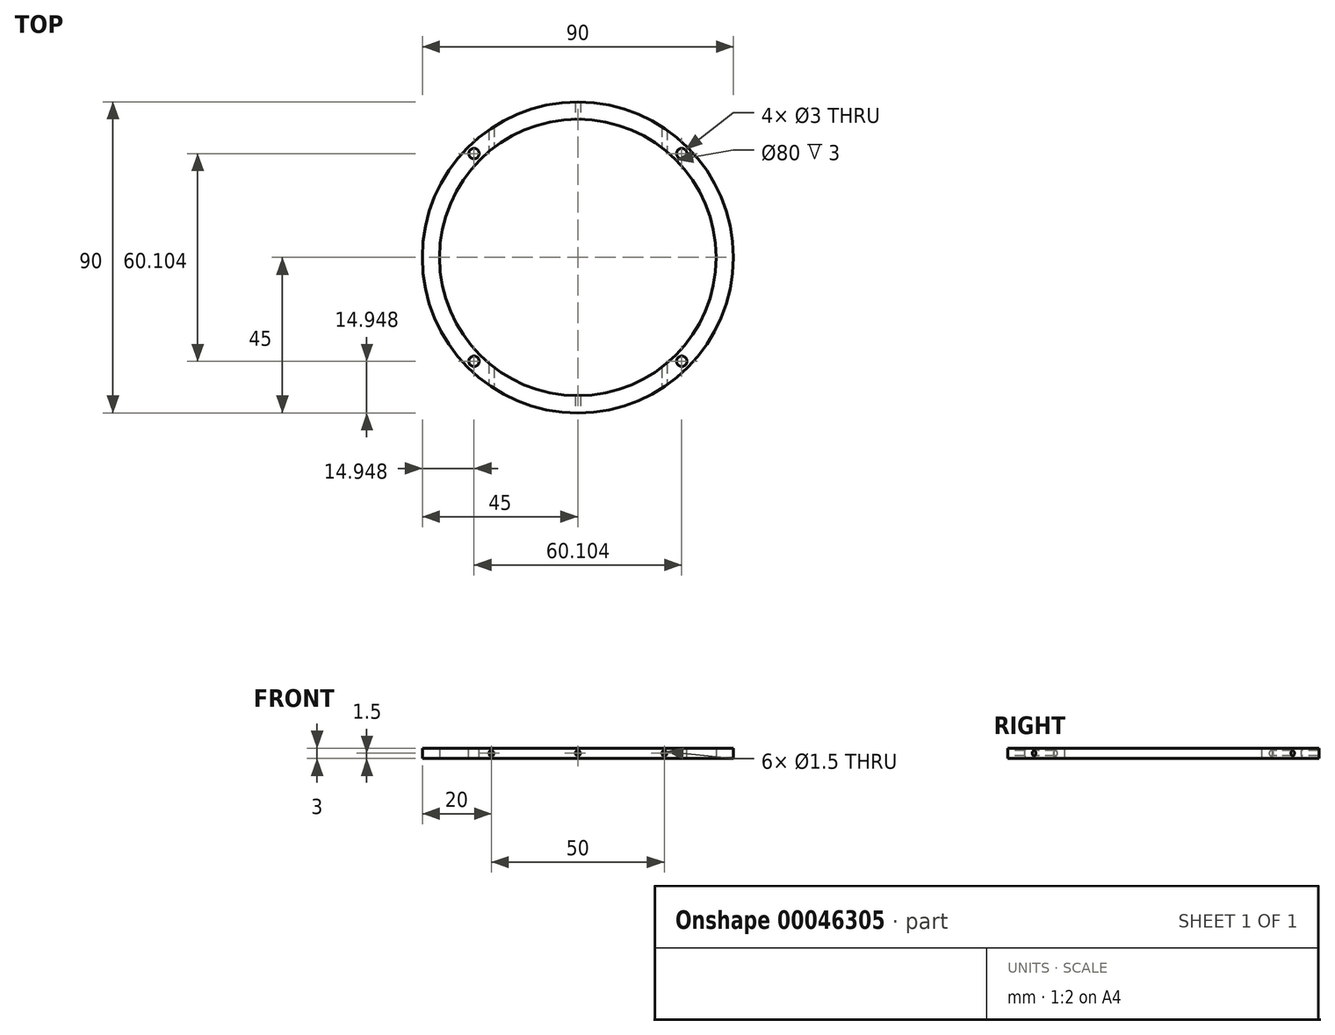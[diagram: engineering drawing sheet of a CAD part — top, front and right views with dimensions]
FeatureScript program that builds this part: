
annotation { "Feature Type Name" : "Feature", "Feature Type Description" : "" }
export const myFeature = defineFeature(function(context is Context, id is Id, definition is map)
    precondition{}
    {
        {
            var Q0;
            Q0=qCreatedBy(makeId("Top.planeOp"),FACE);
            var sketch = newSketch(context, id + "F0", { "sketchPlane" : qUnion([Q0])});
            skCircle(sketch, "E0", {"center": v(0, 0) * mm, "radius": 45 * mm});
            skCircle(sketch, "E1", {"center": v(0, 0) * mm, "radius": 40 * mm});
            skSolve(sketch);
        }
        {
            var Q0;
            Q0=qCreatedBy(makeId("Top.planeOp"),FACE);
            cPlane(context, id + "F1", {"entities" : qUnion([Q0]), "cplaneType" : CPlaneType.OFFSET, "offset" : 1.5 * mm, "width" : 150 * mm, "height" : 150 * mm});
        }
        {
            var Q0;
            Q0=makeQuery(id+"F0.imprint","IMPRINT",FACE,{"disambiguationData":[TD([[makeQuery(id+"F0.imprint","IMPRINT",EDGE,{"derivedFrom":sQuery(id+"F0.wireOp",EDGE,"E0")}),1.0]])]});
            extrude(context, id + "F2", {"entities" : qUnion([Q0]), "depth" : 3 * mm});
        }
        {
            var Q0;
            Q0=qCreatedBy(id+"F1.planeOp",FACE);
            var sketch = newSketch(context, id + "F3", { "sketchPlane" : qUnion([Q0])});
            skLineSegment(sketch, "E2.bottom", {"start": v(-0.75, 45) * mm, "end": v(0.75, 45) * mm});
            skLineSegment(sketch, "E2.top", {"start": v(-0.75, -45) * mm, "end": v(0.75, -45) * mm});
            skLineSegment(sketch, "E2.left", {"start": v(-0.75, 45) * mm, "end": v(-0.75, -45) * mm});
            skLineSegment(sketch, "E2.right", {"start": v(0.75, 45) * mm, "end": v(0.75, -45) * mm});
            skLineSegment(sketch, "E3.1.0.0", {"start": v(-24.25, 45) * mm, "end": v(-24.25, -45) * mm});
            skLineSegment(sketch, "E3.1.0.1", {"start": v(-25.75, 45) * mm, "end": v(-25.75, -45) * mm});
            skLineSegment(sketch, "E3.1.0.2", {"start": v(-25.75, -45) * mm, "end": v(-24.25, -45) * mm});
            skLineSegment(sketch, "E3.1.0.3", {"start": v(-25.75, 45) * mm, "end": v(-24.25, 45) * mm});
            skLineSegment(sketch, "E3.direction1", {"start": v(-24.25, -45) * mm, "end": v(0.75, -45) * mm, "construction": true});
            skLineSegment(sketch, "E4.1.0.0", {"start": v(24.25, 45) * mm, "end": v(24.25, -45) * mm});
            skLineSegment(sketch, "E4.1.0.1", {"start": v(25.75, 45) * mm, "end": v(25.75, -45) * mm});
            skLineSegment(sketch, "E4.1.0.2", {"start": v(24.25, 45) * mm, "end": v(25.75, 45) * mm});
            skLineSegment(sketch, "E4.1.0.3", {"start": v(24.25, -45) * mm, "end": v(25.75, -45) * mm});
            skLineSegment(sketch, "E4.direction1", {"start": v(-0.75, -45) * mm, "end": v(24.25, -45) * mm, "construction": true});
            skSolve(sketch);
        }
        {
            var Q0;
            {var subQ0=sQuery(id+"F0.wireOp",EDGE,"E0");var subQ1=sQuery(id+"F0.wireOp",EDGE,"E1");Q0=makeQuery(id+"F0FMnj3Zhg4bKZp_1.boolean.opBoolean","SPLIT",FACE,{"disambiguationData":[TD([makeQuery(id+"F2.opExtrude","SWEPT_FACE",FACE,{"disambiguationData":[OSD([subQ0])]}),makeQuery(id+"F2.opExtrude","SWEPT_FACE",FACE,{"disambiguationData":[OSD([subQ1])]}),makeQuery(id+"F0FMnj3Zhg4bKZp_1.opExtrude","SWEPT_FACE",FACE,{"disambiguationData":[OSD([sQuery(id+"F3.wireOp",EDGE,"E3.1.0.1")])]})])],"derivedFrom":makeQuery(id+"F2.opExtrude","CAP_FACE",FACE,{"disambiguationData":[OSD([subQ0,subQ1])],"isStart":false})});}
            var sketch = newSketch(context, id + "F4", { "sketchPlane" : qUnion([Q0])});
            skCircle(sketch, "E5", {"center": v(0, 0) * mm, "radius": 42.5 * mm, "construction": true});
            skLineSegment(sketch, "E6", {"start": v(-30.05, 30.05) * mm, "end": v(30.05, -30.05) * mm, "construction": true});
            skLineSegment(sketch, "E7", {"start": v(-30.05, -30.05) * mm, "end": v(30.05, 30.05) * mm, "construction": true});
            skSolve(sketch);
        }
        {
            var Q0;
            Q0=sQuery(id+"F4.wireOp",VERTEX,"E6.start");
            var Q1;
            Q1=sQuery(id+"F4.wireOp",VERTEX,"E7.start");
            var Q2;
            Q2=sQuery(id+"F4.wireOp",VERTEX,"E6.end");
            var Q3;
            Q3=sQuery(id+"F4.wireOp",VERTEX,"E7.end");
            var Q4;
            Q4=makeQuery(id+"F2.opExtrude","SWEPT_BODY",BODY,{"disambiguationData":[OSD([sQuery(id+"F0.wireOp",EDGE,"E0"),sQuery(id+"F0.wireOp",EDGE,"E1")])]});
            hole(context, id + "F5", {"style" : HoleStyle.SIMPLE, "holeDiameter" : 3 * mm, "endStyle" : HoleEndStyle.THROUGH, "locations" : qUnion([Q0, Q1, Q2, Q3]), "scope" : qUnion([Q4])});
        }
        {
            var Q0;
            Q0=qCreatedBy(makeId("Front.planeOp"),FACE);
            var sketch = newSketch(context, id + "F6", { "sketchPlane" : qUnion([Q0])});
            skPoint(sketch, "E8", {"position": v(0, 1.5) * mm});
            skPoint(sketch, "E9", {"position": v(-25, 1.5) * mm});
            skPoint(sketch, "E10", {"position": v(25, 1.5) * mm});
            skCircle(sketch, "E11", {"center": v(-25, 1.5) * mm, "radius": 0.75 * mm});
            skCircle(sketch, "E12", {"center": v(0, 1.5) * mm, "radius": 0.75 * mm});
            skCircle(sketch, "E13", {"center": v(25, 1.5) * mm, "radius": 0.75 * mm});
            skSolve(sketch);
        }
        {
            var Q0;
            Q0 = qSketchRegion(id + "F6", true);
            extrude(context, id + "F7", {"entities" : qUnion([Q0]), "operationType" : NewBodyOperationType.REMOVE, "endBound" : BoundingType.SYMMETRIC, "oppositeDirection" : true, "depth" : 100 * mm});
        }
    });
